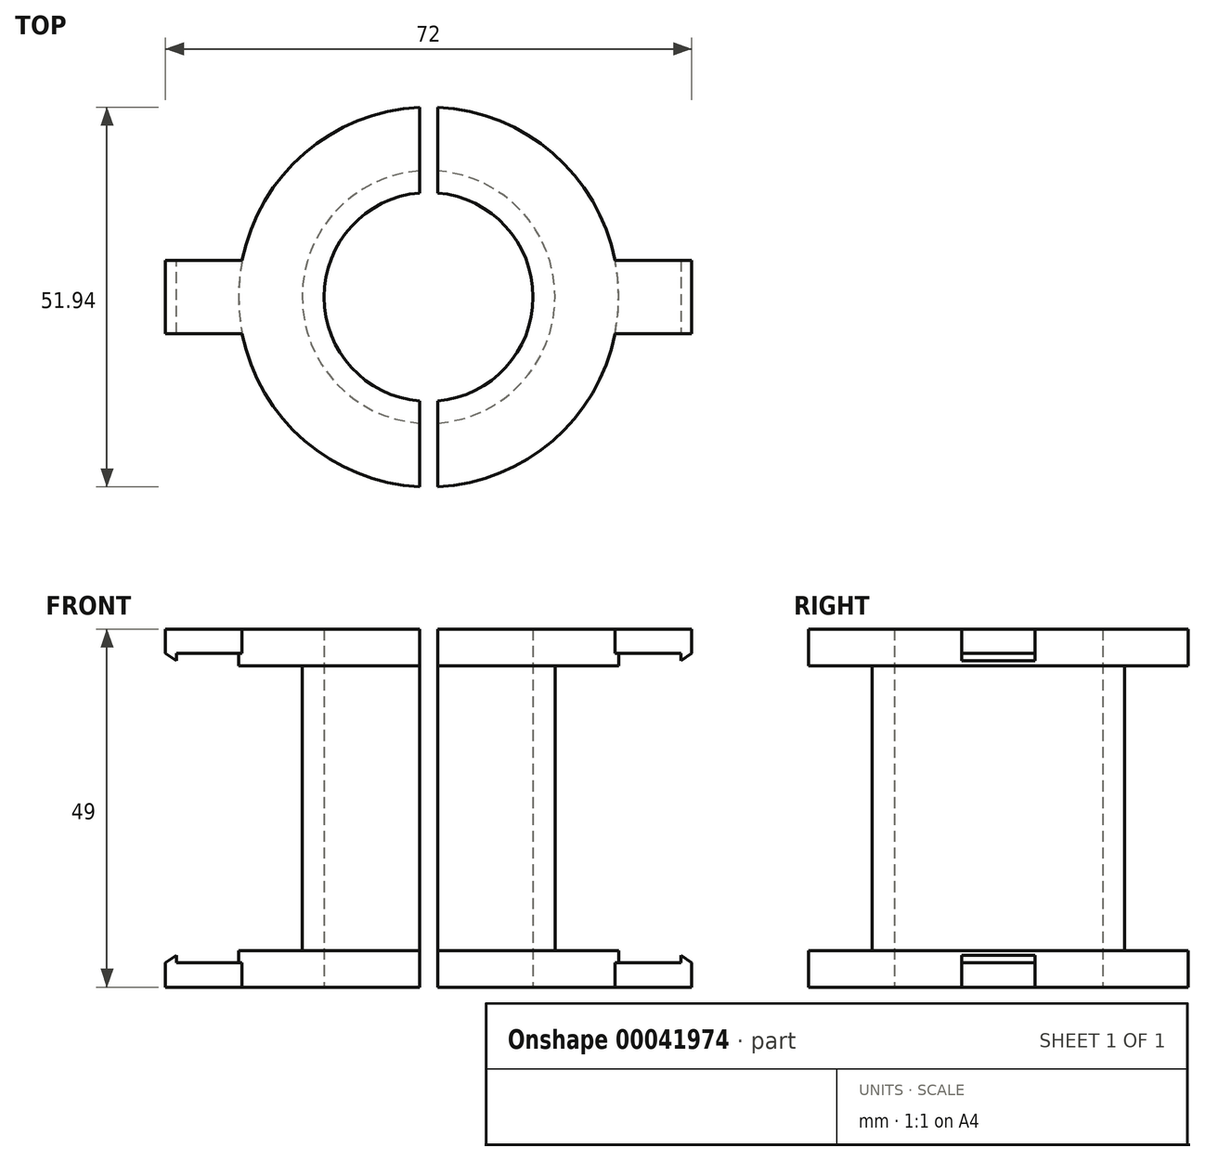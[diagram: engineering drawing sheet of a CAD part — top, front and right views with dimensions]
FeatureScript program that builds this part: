
annotation { "Feature Type Name" : "Feature", "Feature Type Description" : "" }
export const myFeature = defineFeature(function(context is Context, id is Id, definition is map)
    precondition{}
    {
        {
            var Q0;
            Q0=qCreatedBy(makeId("Top.planeOp"),FACE);
            var sketch = newSketch(context, id + "F0", { "sketchPlane" : qUnion([Q0])});
            skCircle(sketch, "E0", {"center": v(0, 0) * mm, "radius": 26 * mm});
            skCircle(sketch, "E1", {"center": v(0, 0) * mm, "radius": 14.3 * mm});
            skLineSegment(sketch, "E2", {"start": v(0, 0) * mm, "end": v(0, 5) * mm, "construction": true});
            skLineSegment(sketch, "E3", {"start": v(0, 0) * mm, "end": v(0, -5) * mm, "construction": true});
            skLineSegment(sketch, "E4", {"start": v(-26, 0) * mm, "end": v(-36, 0) * mm, "construction": true});
            skLineSegment(sketch, "E5", {"start": v(-36, -5) * mm, "end": v(-36, 0) * mm});
            skLineSegment(sketch, "E6", {"start": v(-36, 0) * mm, "end": v(-36, 5) * mm});
            skLineSegment(sketch, "E7", {"start": v(-36, 5) * mm, "end": v(-25.51, 5) * mm});
            skLineSegment(sketch, "E8.trimOffspring", {"start": v(-25.51, -5) * mm, "end": v(-36, -5) * mm});
            skLineSegment(sketch, "E9.MirrorCS", {"start": v(36, 0) * mm, "end": v(36, 5) * mm});
            skLineSegment(sketch, "E10.MirrorCS", {"start": v(36, -5) * mm, "end": v(36, 0) * mm});
            skLineSegment(sketch, "E11.MirrorCS", {"start": v(25.51, -5) * mm, "end": v(36, -5) * mm});
            skLineSegment(sketch, "E12.MirrorCS", {"start": v(36, 5) * mm, "end": v(25.51, 5) * mm});
            skLineSegment(sketch, "E13", {"start": v(-36, 0) * mm, "end": v(-34.5, 0) * mm, "construction": true});
            skLineSegment(sketch, "E14", {"start": v(-34.5, 0) * mm, "end": v(-34.5, 5) * mm});
            skLineSegment(sketch, "E15", {"start": v(-34.5, 0) * mm, "end": v(-34.5, -5) * mm});
            skLineSegment(sketch, "E16.MirrorCS", {"start": v(34.5, 0) * mm, "end": v(34.5, 5) * mm});
            skLineSegment(sketch, "E17.MirrorCS", {"start": v(34.5, 0) * mm, "end": v(34.5, -5) * mm});
            skLineSegment(sketch, "E18", {"start": v(0, 0) * mm, "end": v(1.25, 0) * mm, "construction": true});
            skLineSegment(sketch, "E19", {"start": v(0, 0) * mm, "end": v(-1.25, 0) * mm, "construction": true});
            skLineSegment(sketch, "E20", {"start": v(1.25, 0) * mm, "end": v(1.25, 25.97) * mm});
            skLineSegment(sketch, "E21", {"start": v(-1.25, 0) * mm, "end": v(-1.25, 25.97) * mm});
            skLineSegment(sketch, "E22.MirrorCS", {"start": v(1.25, 0) * mm, "end": v(1.25, -25.97) * mm});
            skLineSegment(sketch, "E23.MirrorCS", {"start": v(-1.25, 0) * mm, "end": v(-1.25, -25.97) * mm});
            skCircle(sketch, "E24", {"center": v(0, 0) * mm, "radius": 17.3 * mm});
            skLineSegment(sketch, "E25", {"start": v(14.3, 0) * mm, "end": v(17.3, 0) * mm, "construction": true});
            skSolve(sketch);
        }
        {
            var Q0;
            {var subQ3=sQuery(id+"F0.wireOp",EDGE,"E0");var subQ6=makeQuery(id+"F0.imprint","INTERSECT",VERTEX,{"derivedFrom":[subQ3,sQuery(id+"F0.wireOp",EDGE,"E7")]});Q0=makeQuery(id+"F0.imprint","IMPRINT",FACE,{"disambiguationData":[TD([[makeQuery(id+"F0.imprint","IMPRINT",EDGE,{"disambiguationData":[TD([[subQ6,1.0]])],"derivedFrom":subQ3}),1.0]])]});}
            var Q1;
            {var subQ3=sQuery(id+"F0.wireOp",EDGE,"E0");var subQ8=makeQuery(id+"F0.imprint","INTERSECT",VERTEX,{"derivedFrom":[subQ3,sQuery(id+"F0.wireOp",EDGE,"E12.MirrorCS")]});Q1=makeQuery(id+"F0.imprint","IMPRINT",FACE,{"disambiguationData":[TD([[makeQuery(id+"F0.imprint","IMPRINT",EDGE,{"disambiguationData":[TD([[subQ8,-1.0]])],"derivedFrom":subQ3}),1.0]])]});}
            var Q2;
            {var subQ3=sQuery(id+"F0.wireOp",EDGE,"E0");var subQ5=sQuery(id+"F0.wireOp",EDGE,"E20");var subQ7=makeQuery(id+"F0.imprint","INTERSECT",VERTEX,{"derivedFrom":[subQ3,subQ5]});Q2=makeQuery(id+"F0.imprint","IMPRINT",FACE,{"disambiguationData":[TD([[makeQuery(id+"F0.imprint","IMPRINT",EDGE,{"disambiguationData":[TD([[subQ7,-1.0]])],"derivedFrom":subQ3}),1.0]])]});}
            var Q3;
            {var subQ0=sQuery(id+"F0.wireOp",EDGE,"E22.MirrorCS");var subQ3=sQuery(id+"F0.wireOp",EDGE,"E0");var subQ4=makeQuery(id+"F0.imprint","INTERSECT",VERTEX,{"derivedFrom":[subQ3,subQ0]});Q3=makeQuery(id+"F0.imprint","IMPRINT",FACE,{"disambiguationData":[TD([[makeQuery(id+"F0.imprint","IMPRINT",EDGE,{"disambiguationData":[TD([[subQ4,1.0]])],"derivedFrom":subQ3}),1.0]])]});}
            var Q4;
            {var subQ3=sQuery(id+"F0.wireOp",EDGE,"E1");var subQ5=sQuery(id+"F0.wireOp",EDGE,"E21");var subQ7=makeQuery(id+"F0.imprint","INTERSECT",VERTEX,{"derivedFrom":[subQ3,subQ5]});Q4=makeQuery(id+"F0.imprint","IMPRINT",FACE,{"disambiguationData":[TD([[makeQuery(id+"F0.imprint","IMPRINT",EDGE,{"disambiguationData":[TD([[subQ7,-1.0]])],"derivedFrom":subQ3}),-1.0]])]});}
            var Q5;
            {var subQ3=sQuery(id+"F0.wireOp",EDGE,"E1");var subQ5=sQuery(id+"F0.wireOp",EDGE,"E20");var subQ7=makeQuery(id+"F0.imprint","INTERSECT",VERTEX,{"derivedFrom":[subQ3,subQ5]});Q5=makeQuery(id+"F0.imprint","IMPRINT",FACE,{"disambiguationData":[TD([[makeQuery(id+"F0.imprint","IMPRINT",EDGE,{"disambiguationData":[TD([[subQ7,1.0]])],"derivedFrom":subQ3}),-1.0]])]});}
            var Q6;
            {var subQ1=sQuery(id+"F0.wireOp",EDGE,"E23.MirrorCS");var subQ5=sQuery(id+"F0.wireOp",EDGE,"E1");var subQ6=makeQuery(id+"F0.imprint","INTERSECT",VERTEX,{"derivedFrom":[subQ5,subQ1]});Q6=makeQuery(id+"F0.imprint","IMPRINT",FACE,{"disambiguationData":[TD([[makeQuery(id+"F0.imprint","IMPRINT",EDGE,{"disambiguationData":[TD([[subQ6,-1.0]])],"derivedFrom":subQ5}),-1.0]])]});}
            var Q7;
            {var subQ0=sQuery(id+"F0.wireOp",EDGE,"E21");var subQ3=sQuery(id+"F0.wireOp",EDGE,"E1");var subQ4=makeQuery(id+"F0.imprint","INTERSECT",VERTEX,{"derivedFrom":[subQ3,subQ0]});Q7=makeQuery(id+"F0.imprint","IMPRINT",FACE,{"disambiguationData":[TD([[makeQuery(id+"F0.imprint","IMPRINT",EDGE,{"disambiguationData":[TD([[subQ4,1.0]])],"derivedFrom":subQ3}),-1.0]])]});}
            extrude(context, id + "F1", {"entities" : qUnion([Q0, Q1, Q2, Q3, Q4, Q5, Q6, Q7]), "depth" : 5 * mm});
        }
        {
            var Q0;
            {var subQ1=sQuery(id+"F0.wireOp",EDGE,"E14");Q0=makeQuery(id+"F0.imprint","IMPRINT",FACE,{"disambiguationData":[TD([[makeQuery(id+"F0.imprint","IMPRINT",EDGE,{"derivedFrom":subQ1}),-1.0]])]});}
            var Q1;
            {var subQ0=sQuery(id+"F0.wireOp",EDGE,"E5");Q1=makeQuery(id+"F0.imprint","IMPRINT",FACE,{"disambiguationData":[TD([[makeQuery(id+"F0.imprint","IMPRINT",EDGE,{"derivedFrom":subQ0}),-1.0]])]});}
            var Q2;
            {var subQ6=sQuery(id+"F0.wireOp",EDGE,"E16.MirrorCS");Q2=makeQuery(id+"F0.imprint","IMPRINT",FACE,{"disambiguationData":[TD([[makeQuery(id+"F0.imprint","IMPRINT",EDGE,{"derivedFrom":subQ6}),1.0]])]});}
            var Q3;
            {var subQ2=sQuery(id+"F0.wireOp",EDGE,"E9.MirrorCS");Q3=makeQuery(id+"F0.imprint","IMPRINT",FACE,{"disambiguationData":[TD([[makeQuery(id+"F0.imprint","IMPRINT",EDGE,{"derivedFrom":subQ2}),1.0]])]});}
            extrude(context, id + "F2", {"entities" : qUnion([Q0, Q1, Q2, Q3]), "operationType" : NewBodyOperationType.ADD, "depth" : 3.33 * mm});
        }
        {
            var Q0;
            {var subQ0=sQuery(id+"F0.wireOp",EDGE,"E5");Q0=makeQuery(id+"F0.imprint","IMPRINT",FACE,{"disambiguationData":[TD([[makeQuery(id+"F0.imprint","IMPRINT",EDGE,{"derivedFrom":subQ0}),-1.0]])]});}
            var Q1;
            {var subQ2=sQuery(id+"F0.wireOp",EDGE,"E9.MirrorCS");Q1=makeQuery(id+"F0.imprint","IMPRINT",FACE,{"disambiguationData":[TD([[makeQuery(id+"F0.imprint","IMPRINT",EDGE,{"derivedFrom":subQ2}),1.0]])]});}
            extrude(context, id + "F3", {"entities" : qUnion([Q0, Q1]), "operationType" : NewBodyOperationType.ADD, "depth" : 4.33 * mm});
        }
        {
            var Q0;
            {var subQ0=sQuery(id+"F0.wireOp",EDGE,"E8.trimOffspring");Q0=makeQuery(id+"F3.boolean.opBoolean","MERGE",FACE,{"derivedFrom":[makeQuery(id+"F2.opExtrude","SWEPT_FACE",FACE,{"disambiguationData":[OSD([subQ0])]}),makeQuery(id+"F3.opExtrude","SWEPT_FACE",FACE,{"disambiguationData":[OSD([subQ0])]})]});}
            var sketch = newSketch(context, id + "F4", { "sketchPlane" : qUnion([Q0])});
            skLineSegment(sketch, "E26", {"start": v(-34.5, 4.33) * mm, "end": v(-36, 3.33) * mm});
            skSolve(sketch);
        }
        {
            var Q0;
            {var subQ0=sQuery(id+"F0.wireOp",EDGE,"E11.MirrorCS");Q0=makeQuery(id+"F3.boolean.opBoolean","MERGE",FACE,{"derivedFrom":[makeQuery(id+"F2.opExtrude","SWEPT_FACE",FACE,{"disambiguationData":[OSD([subQ0])]}),makeQuery(id+"F3.opExtrude","SWEPT_FACE",FACE,{"disambiguationData":[OSD([subQ0])]})]});}
            var sketch = newSketch(context, id + "F5", { "sketchPlane" : qUnion([Q0])});
            skLineSegment(sketch, "E27", {"start": v(34.5, 4.33) * mm, "end": v(36, 3.33) * mm});
            skSolve(sketch);
        }
        {
            var Q0;
            {var subQ3=sQuery(id+"F4.wireOp",EDGE,"E26");Q0=makeQuery(id+"F4.imprint","IMPRINT",FACE,{"disambiguationData":[TD([[makeQuery(id+"F4.imprint","IMPRINT",EDGE,{"derivedFrom":subQ3}),-1.0]])]});}
            var Q1;
            {var subQ3=sQuery(id+"F5.wireOp",EDGE,"E27");Q1=makeQuery(id+"F5.imprint","IMPRINT",FACE,{"disambiguationData":[TD([[makeQuery(id+"F5.imprint","IMPRINT",EDGE,{"derivedFrom":subQ3}),1.0]])]});}
            var Q2;
            {var subQ0=sQuery(id+"F0.wireOp",EDGE,"E7");Q2=makeQuery(id+"F3.boolean.opBoolean","MERGE",FACE,{"derivedFrom":[makeQuery(id+"F2.opExtrude","SWEPT_FACE",FACE,{"disambiguationData":[OSD([subQ0])]}),makeQuery(id+"F3.opExtrude","SWEPT_FACE",FACE,{"disambiguationData":[OSD([subQ0])]})]});}
            extrude(context, id + "F6", {"entities" : qUnion([Q0, Q1]), "operationType" : NewBodyOperationType.REMOVE, "endBound" : BoundingType.UP_TO_SURFACE, "oppositeDirection" : true, "endBoundEntityFace" : qUnion([Q2]), "depth" : 25 * mm});
        }
        {
            var Q0;
            {var subQ3=sQuery(id+"F0.wireOp",EDGE,"E1");var subQ5=sQuery(id+"F0.wireOp",EDGE,"E21");var subQ7=makeQuery(id+"F0.imprint","INTERSECT",VERTEX,{"derivedFrom":[subQ3,subQ5]});Q0=makeQuery(id+"F0.imprint","IMPRINT",FACE,{"disambiguationData":[TD([[makeQuery(id+"F0.imprint","IMPRINT",EDGE,{"disambiguationData":[TD([[subQ7,-1.0]])],"derivedFrom":subQ3}),-1.0]])]});}
            var Q1;
            {var subQ3=sQuery(id+"F0.wireOp",EDGE,"E1");var subQ5=sQuery(id+"F0.wireOp",EDGE,"E20");var subQ7=makeQuery(id+"F0.imprint","INTERSECT",VERTEX,{"derivedFrom":[subQ3,subQ5]});Q1=makeQuery(id+"F0.imprint","IMPRINT",FACE,{"disambiguationData":[TD([[makeQuery(id+"F0.imprint","IMPRINT",EDGE,{"disambiguationData":[TD([[subQ7,1.0]])],"derivedFrom":subQ3}),-1.0]])]});}
            var Q2;
            {var subQ1=sQuery(id+"F0.wireOp",EDGE,"E23.MirrorCS");var subQ5=sQuery(id+"F0.wireOp",EDGE,"E1");var subQ6=makeQuery(id+"F0.imprint","INTERSECT",VERTEX,{"derivedFrom":[subQ5,subQ1]});Q2=makeQuery(id+"F0.imprint","IMPRINT",FACE,{"disambiguationData":[TD([[makeQuery(id+"F0.imprint","IMPRINT",EDGE,{"disambiguationData":[TD([[subQ6,-1.0]])],"derivedFrom":subQ5}),-1.0]])]});}
            var Q3;
            {var subQ0=sQuery(id+"F0.wireOp",EDGE,"E21");var subQ3=sQuery(id+"F0.wireOp",EDGE,"E1");var subQ4=makeQuery(id+"F0.imprint","INTERSECT",VERTEX,{"derivedFrom":[subQ3,subQ0]});Q3=makeQuery(id+"F0.imprint","IMPRINT",FACE,{"disambiguationData":[TD([[makeQuery(id+"F0.imprint","IMPRINT",EDGE,{"disambiguationData":[TD([[subQ4,1.0]])],"derivedFrom":subQ3}),-1.0]])]});}
            extrude(context, id + "F7", {"entities" : qUnion([Q0, Q1, Q2, Q3]), "operationType" : NewBodyOperationType.ADD, "depth" : 24.5 * mm});
        }
        {
            var Q0;
            Q0=makeQuery(id+"F1.opExtrude","SWEPT_BODY",BODY,{"disambiguationData":[OSD([sQuery(id+"F0.wireOp",EDGE,"E0"),sQuery(id+"F0.wireOp",EDGE,"E1")])]});
            var Q1;
            Q1=makeQuery(id+"F7.opExtrude","CAP_FACE",FACE,{"disambiguationData":[OSD([sQuery(id+"F0.wireOp",EDGE,"E1"),sQuery(id+"F0.wireOp",EDGE,"E24")])],"isStart":false});
            mirror(context, id + "F8", {"operationType" : NewBodyOperationType.ADD, "entities" : qUnion([Q0]), "mirrorPlane" : qUnion([Q1])});
        }
        {
            var Q0;
            {var subQ0=sQuery(id+"F0.wireOp",EDGE,"E22.MirrorCS");var subQ3=sQuery(id+"F0.wireOp",EDGE,"E0");var subQ4=makeQuery(id+"F0.imprint","INTERSECT",VERTEX,{"derivedFrom":[subQ3,subQ0]});Q0=makeQuery(id+"F0.imprint","IMPRINT",FACE,{"disambiguationData":[TD([[makeQuery(id+"F0.imprint","IMPRINT",EDGE,{"disambiguationData":[TD([[subQ4,1.0]])],"derivedFrom":subQ3}),1.0]])]});}
            var Q1;
            {var subQ3=sQuery(id+"F0.wireOp",EDGE,"E0");var subQ5=sQuery(id+"F0.wireOp",EDGE,"E20");var subQ7=makeQuery(id+"F0.imprint","INTERSECT",VERTEX,{"derivedFrom":[subQ3,subQ5]});Q1=makeQuery(id+"F0.imprint","IMPRINT",FACE,{"disambiguationData":[TD([[makeQuery(id+"F0.imprint","IMPRINT",EDGE,{"disambiguationData":[TD([[subQ7,-1.0]])],"derivedFrom":subQ3}),1.0]])]});}
            var Q2;
            {var subQ1=sQuery(id+"F0.wireOp",EDGE,"E23.MirrorCS");var subQ5=sQuery(id+"F0.wireOp",EDGE,"E1");var subQ6=makeQuery(id+"F0.imprint","INTERSECT",VERTEX,{"derivedFrom":[subQ5,subQ1]});Q2=makeQuery(id+"F0.imprint","IMPRINT",FACE,{"disambiguationData":[TD([[makeQuery(id+"F0.imprint","IMPRINT",EDGE,{"disambiguationData":[TD([[subQ6,-1.0]])],"derivedFrom":subQ5}),-1.0]])]});}
            var Q3;
            {var subQ0=sQuery(id+"F0.wireOp",EDGE,"E21");var subQ3=sQuery(id+"F0.wireOp",EDGE,"E1");var subQ4=makeQuery(id+"F0.imprint","INTERSECT",VERTEX,{"derivedFrom":[subQ3,subQ0]});Q3=makeQuery(id+"F0.imprint","IMPRINT",FACE,{"disambiguationData":[TD([[makeQuery(id+"F0.imprint","IMPRINT",EDGE,{"disambiguationData":[TD([[subQ4,1.0]])],"derivedFrom":subQ3}),-1.0]])]});}
            extrude(context, id + "F9", {"entities" : qUnion([Q0, Q1, Q2, Q3]), "operationType" : NewBodyOperationType.REMOVE, "endBound" : BoundingType.THROUGH_ALL, "depth" : 25 * mm});
        }
    });
